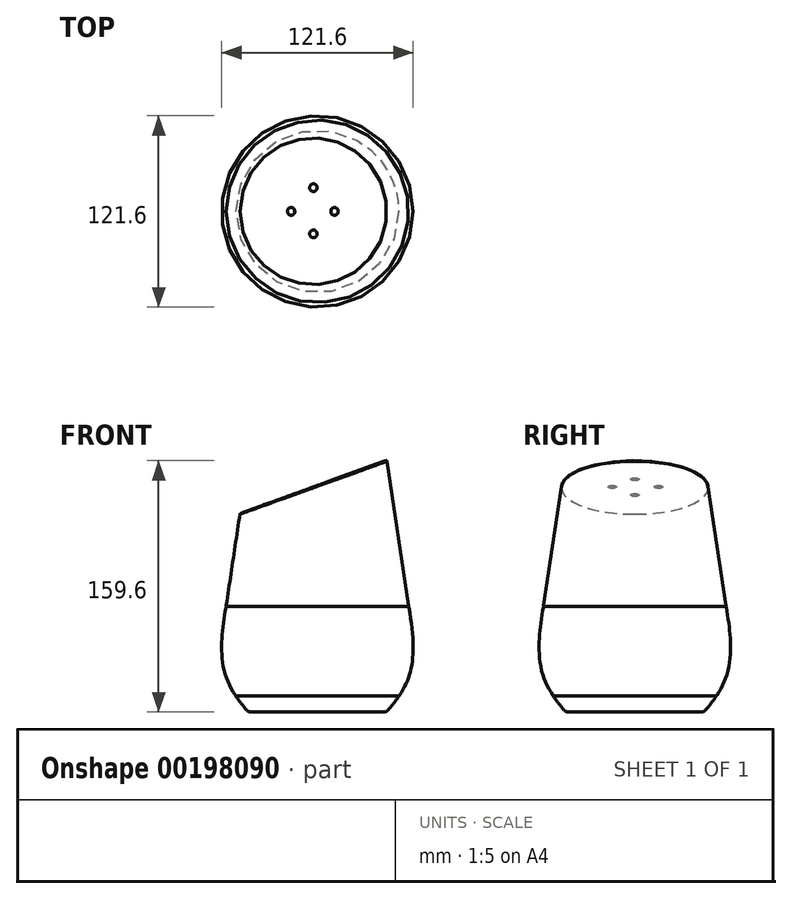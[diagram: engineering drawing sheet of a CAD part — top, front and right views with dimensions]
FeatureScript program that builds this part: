
annotation { "Feature Type Name" : "Feature", "Feature Type Description" : "" }
export const myFeature = defineFeature(function(context is Context, id is Id, definition is map)
    precondition{}
    {
        {
            var Q0;
            Q0=qCreatedBy(makeId("Front.planeOp"),FACE);
            var sketch = newSketch(context, id + "F0", { "sketchPlane" : qUnion([Q0])});
            skLineSegment(sketch, "E0", {"start": v(0, 171.12) * mm, "end": v(0, -72.98) * mm, "construction": true});
            skLineSegment(sketch, "E1", {"start": v(0, 160) * mm, "end": v(-44, 160) * mm});
            skLineSegment(sketch, "E2", {"start": v(-44, 160) * mm, "end": v(-58, 67) * mm});
            skLineSegment(sketch, "E3", {"start": v(-44, 0) * mm, "end": v(0, 0) * mm});
            skFitSpline(sketch, "E4", {"points": [v(-44, 0) * mm, v(-58, 67) * mm], "startDerivative": vector(-48.49, 56.39) * mm, "endDerivative": vector(18.84, 106.53) * mm});
            skLineSegment(sketch, "E5", {"start": v(0, 160) * mm, "end": v(0, 0) * mm});
            skSolve(sketch);
        }
        {
            var Q0;
            Q0 = qSketchRegion(id + "F0", true);
            var Q1;
            Q1=sQuery(id+"F0.wireOp",EDGE,"E5");
            revolve(context, id + "F1", {"entities" : qUnion([Q0]), "axis" : qUnion([Q1]), "revolveType" : RevolveType.FULL});
        }
        {
            var Q0;
            Q0=qCreatedBy(makeId("Front.planeOp"),FACE);
            var sketch = newSketch(context, id + "F2", { "sketchPlane" : qUnion([Q0])});
            skLineSegment(sketch, "E6", {"start": v(46.4, 160.64) * mm, "end": v(-49.8, 160.64) * mm});
            skLineSegment(sketch, "E7", {"start": v(-49.8, 160.64) * mm, "end": v(-49.8, 125.64) * mm});
            skLineSegment(sketch, "E8", {"start": v(-49.8, 125.64) * mm, "end": v(46.4, 160.64) * mm});
            skLineSegment(sketch, "E9.bottom", {"start": v(-60.77, 67.1) * mm, "end": v(63.1, 67.1) * mm});
            skLineSegment(sketch, "E9.top", {"start": v(-60.77, 66.9) * mm, "end": v(63.1, 66.9) * mm});
            skLineSegment(sketch, "E9.left", {"start": v(-60.77, 67.1) * mm, "end": v(-60.77, 66.9) * mm});
            skLineSegment(sketch, "E9.right", {"start": v(63.1, 67.1) * mm, "end": v(63.1, 66.9) * mm});
            skLineSegment(sketch, "E10.bottom", {"start": v(54.38, 10.2) * mm, "end": v(-52.4, 10.2) * mm});
            skLineSegment(sketch, "E10.top", {"start": v(54.38, 10) * mm, "end": v(-52.4, 10) * mm});
            skLineSegment(sketch, "E10.left", {"start": v(54.38, 10.2) * mm, "end": v(54.38, 10) * mm});
            skLineSegment(sketch, "E10.right", {"start": v(-52.4, 10.2) * mm, "end": v(-52.4, 10) * mm});
            skSolve(sketch);
        }
        {
            var Q0;
            Q0 = qSketchRegion(id + "F2", true);
            extrude(context, id + "F3", {"entities" : qUnion([Q0]), "operationType" : NewBodyOperationType.REMOVE, "endBound" : BoundingType.THROUGH_ALL, "oppositeDirection" : true, "depth" : 25 * mm, "hasSecondDirection" : true, "secondDirectionBound" : SecondDirectionBoundingType.THROUGH_ALL, "secondDirectionOppositeDirection" : false, "secondDirectionDepth" : 25 * mm});
        }
        {
            var Q0;
            Q0=makeQuery(id+"F3.boolean.opBoolean","COPY",FACE,{"derivedFrom":makeQuery(id+"F3.opExtrude","SWEPT_FACE",FACE,{"disambiguationData":[OSD([sQuery(id+"F2.wireOp",EDGE,"E8")])]})});
            var sketch = newSketch(context, id + "F4", { "sketchPlane" : qUnion([Q0])});
            skLineSegment(sketch, "E11", {"start": v(96, 0) * mm, "end": v(-3.14, 0) * mm, "construction": true});
            skLineSegment(sketch, "E12", {"start": v(46.44, 46.52) * mm, "end": v(46.44, -46.52) * mm, "construction": true});
            skCircle(sketch, "E13", {"center": v(60.72, 0) * mm, "radius": 2.5 * mm});
            skCircle(sketch, "E14", {"center": v(46.44, 15.05) * mm, "radius": 2.5 * mm});
            skCircle(sketch, "E15", {"center": v(31.38, 0) * mm, "radius": 2.5 * mm});
            skCircle(sketch, "E16", {"center": v(46.44, -14.28) * mm, "radius": 2.5 * mm});
            skLineSegment(sketch, "E17", {"start": v(46.44, 15.05) * mm, "end": v(60.72, 0) * mm, "construction": true});
            skLineSegment(sketch, "E18", {"start": v(46.44, 15.05) * mm, "end": v(31.38, 0) * mm, "construction": true});
            skLineSegment(sketch, "E19", {"start": v(60.72, 0) * mm, "end": v(46.44, -14.28) * mm, "construction": true});
            skLineSegment(sketch, "E20", {"start": v(46.44, -14.28) * mm, "end": v(31.38, 0) * mm, "construction": true});
            skSolve(sketch);
        }
        {
            var Q0;
            Q0 = qSketchRegion(id + "F4", true);
            extrude(context, id + "F5", {"entities" : qUnion([Q0]), "depth" : 0.1 * mm});
        }
        {
            var Q0;
            Q0=makeQuery(id+"F3.boolean.opBoolean","INTERSECT",EDGE,{"derivedFrom":[makeQuery(id+"F1.opRevolve","SWEPT_FACE",FACE,{"disambiguationData":[OSD([sQuery(id+"F0.wireOp",EDGE,"E4")])]}),makeQuery(id+"F3.opExtrude","SWEPT_FACE",FACE,{"disambiguationData":[OSD([sQuery(id+"F2.wireOp",EDGE,"E9.top")])]})]});
            fillet(context, id + "F6", {"entities" : qUnion([Q0]), "radius" : 0.6 * mm, "tangentPropagation" : true, "allowEdgeOverflow" : false});
        }
        {
            var Q0;
            Q0=makeQuery(id+"F3.boolean.opBoolean","INTERSECT",EDGE,{"derivedFrom":[makeQuery(id+"F1.opRevolve","SWEPT_FACE",FACE,{"disambiguationData":[OSD([sQuery(id+"F0.wireOp",EDGE,"E4")])]}),makeQuery(id+"F3.opExtrude","SWEPT_FACE",FACE,{"disambiguationData":[OSD([sQuery(id+"F2.wireOp",EDGE,"E10.top")])]})]});
            fillet(context, id + "F7", {"entities" : qUnion([Q0]), "radius" : 0.2 * mm, "tangentPropagation" : true, "allowEdgeOverflow" : false});
        }
        {
            var Q0;
            Q0=makeQuery(id+"F3.boolean.opBoolean","INTERSECT",EDGE,{"derivedFrom":[makeQuery(id+"F1.opRevolve","SWEPT_FACE",FACE,{"disambiguationData":[OSD([sQuery(id+"F0.wireOp",EDGE,"E4")])]}),makeQuery(id+"F3.opExtrude","SWEPT_FACE",FACE,{"disambiguationData":[OSD([sQuery(id+"F2.wireOp",EDGE,"E10.bottom")])]})]});
            fillet(context, id + "F8", {"entities" : qUnion([Q0]), "radius" : 0.8 * mm, "tangentPropagation" : true, "allowEdgeOverflow" : false});
        }
        {
            var Q0;
            Q0=makeQuery(id+"F3.boolean.opBoolean","INTERSECT",EDGE,{"derivedFrom":[makeQuery(id+"F1.opRevolve","SWEPT_FACE",FACE,{"disambiguationData":[OSD([sQuery(id+"F0.wireOp",EDGE,"E2")])]}),makeQuery(id+"F3.opExtrude","SWEPT_FACE",FACE,{"disambiguationData":[OSD([sQuery(id+"F2.wireOp",EDGE,"E9.bottom")])]})]});
            fillet(context, id + "F9", {"entities" : qUnion([Q0]), "radius" : 0.4 * mm, "tangentPropagation" : true, "allowEdgeOverflow" : false});
        }
        {
            var Q0;
            Q0=makeQuery(id+"F1.opRevolve","SWEPT_EDGE",EDGE,{"disambiguationData":[OSD([sQuery(id+"F0.wireOp",EDGE,"E3"),sQuery(id+"F0.wireOp",EDGE,"E4")])]});
            fillet(context, id + "F10", {"entities" : qUnion([Q0]), "radius" : 3 * mm, "tangentPropagation" : true, "allowEdgeOverflow" : false});
        }
        {
            var Q0;
            Q0=makeQuery(id+"F3.boolean.opBoolean","INTERSECT",EDGE,{"derivedFrom":[makeQuery(id+"F1.opRevolve","SWEPT_FACE",FACE,{"disambiguationData":[OSD([sQuery(id+"F0.wireOp",EDGE,"E2")])]}),makeQuery(id+"F3.opExtrude","SWEPT_FACE",FACE,{"disambiguationData":[OSD([sQuery(id+"F2.wireOp",EDGE,"E8")])]})]});
            fillet(context, id + "F11", {"entities" : qUnion([Q0]), "radius" : 0.5 * mm, "tangentPropagation" : true, "allowEdgeOverflow" : false});
        }
    });
